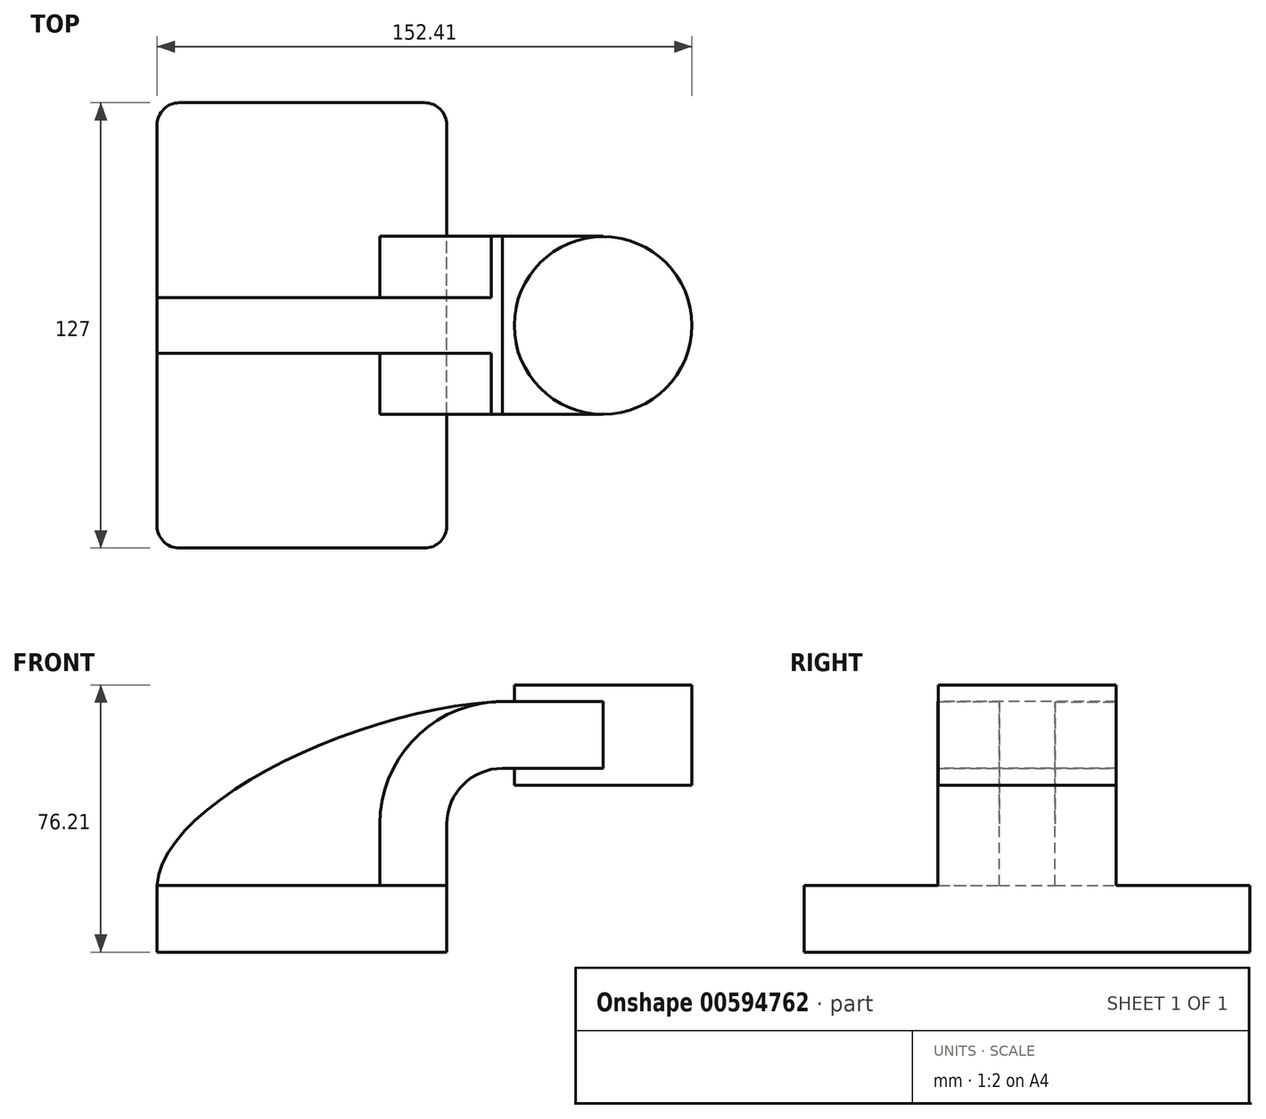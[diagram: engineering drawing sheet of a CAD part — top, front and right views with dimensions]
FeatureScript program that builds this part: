
annotation { "Feature Type Name" : "Feature", "Feature Type Description" : "" }
export const myFeature = defineFeature(function(context is Context, id is Id, definition is map)
    precondition{}
    {
        {
            var Q0;
            Q0=qCreatedBy(makeId("Front.planeOp"),FACE);
            var sketch = newSketch(context, id + "F0", { "sketchPlane" : qUnion([Q0])});
            skLineSegment(sketch, "E0.bottom", {"start": v(41.27, 9.53) * mm, "end": v(-41.28, 9.53) * mm});
            skLineSegment(sketch, "E0.top", {"start": v(41.28, -9.52) * mm, "end": v(-41.27, -9.52) * mm});
            skLineSegment(sketch, "E0.left", {"start": v(41.28, 9.53) * mm, "end": v(41.28, -9.52) * mm});
            skLineSegment(sketch, "E0.right", {"start": v(-41.28, 9.53) * mm, "end": v(-41.27, -9.52) * mm});
            skPoint(sketch, "E0.middle", {"position": v(0, 0) * mm});
            skLineSegment(sketch, "E1.bottom", {"start": v(60.32, 38.1) * mm, "end": v(111.12, 38.1) * mm});
            skLineSegment(sketch, "E1.top", {"start": v(60.32, 66.68) * mm, "end": v(111.12, 66.68) * mm});
            skLineSegment(sketch, "E1.left", {"start": v(60.32, 38.1) * mm, "end": v(60.32, 66.67) * mm});
            skLineSegment(sketch, "E1.right", {"start": v(111.12, 38.1) * mm, "end": v(111.12, 66.68) * mm});
            skPoint(sketch, "E1.middle", {"position": v(85.72, 52.39) * mm});
            skLineSegment(sketch, "E2", {"start": v(41.27, 9.53) * mm, "end": v(41.27, 27) * mm});
            skArc(sketch, "E3", {"start": v(41.27, 27) * mm, "mid": v(45.92, 38.23) * mm, "end": v(57.15, 42.88) * mm});
            skLineSegment(sketch, "E4", {"start": v(57.15, 42.88) * mm, "end": v(85.8, 42.88) * mm});
            skArc(sketch, "E5.0", {"start": v(22.22, 27) * mm, "mid": v(32.45, 51.7) * mm, "end": v(57.15, 61.93) * mm});
            skLineSegment(sketch, "E5.1", {"start": v(22.22, 9.53) * mm, "end": v(22.22, 27) * mm});
            skLineSegment(sketch, "E6.0", {"start": v(57.15, 61.93) * mm, "end": v(85.8, 61.93) * mm});
            skLineSegment(sketch, "E7", {"start": v(85.8, 61.93) * mm, "end": v(85.8, 66.68) * mm});
            skLineSegment(sketch, "E8", {"start": v(85.8, 66.68) * mm, "end": v(85.8, 61.93) * mm});
            skLineSegment(sketch, "E9", {"start": v(85.8, 66.68) * mm, "end": v(85.8, 38.1) * mm});
            skFitSpline(sketch, "E10", {"points": [v(-41.28, 9.53) * mm, v(57.15, 61.93) * mm], "startDerivative": vector(4.3, 72.88) * mm, "endDerivative": vector(115.36, 3.24) * mm});
            skSolve(sketch);
        }
        {
            var Q0;
            Q0=makeQuery(id+"F0.imprint","IMPRINT",FACE,{"disambiguationData":[TD([[makeQuery(id+"F0.imprint","IMPRINT",EDGE,{"derivedFrom":sQuery(id+"F0.wireOp",EDGE,"E0.top")}),-1.0]])]});
            extrude(context, id + "F1", {"entities" : qUnion([Q0]), "endBound" : BoundingType.SYMMETRIC, "depth" : 127 * mm, "offsetDistance" : 25.4 * mm});
        }
        {
            var Q0;
            {var subQ1=sQuery(id+"F0.wireOp",EDGE,"E2");Q0=makeQuery(id+"F0.imprint","IMPRINT",FACE,{"disambiguationData":[TD([[makeQuery(id+"F0.imprint","IMPRINT",EDGE,{"derivedFrom":subQ1}),1.0]])]});}
            var Q1;
            {var subQ0=sQuery(id+"F0.wireOp",EDGE,"E4");var subQ1=sQuery(id+"F0.wireOp",EDGE,"E1.left");var subQ2=makeQuery(id+"F0.imprint","INTERSECT",VERTEX,{"derivedFrom":[subQ1,subQ0]});Q1=makeQuery(id+"F0.imprint","IMPRINT",FACE,{"disambiguationData":[TD([[makeQuery(id+"F0.imprint","IMPRINT",EDGE,{"disambiguationData":[TD([[subQ2,-1.0]])],"derivedFrom":subQ1}),-1.0]])]});}
            extrude(context, id + "F2", {"entities" : qUnion([Q0, Q1]), "operationType" : NewBodyOperationType.ADD, "endBound" : BoundingType.SYMMETRIC, "depth" : 50.8 * mm, "offsetDistance" : 25.4 * mm});
        }
        {
            var Q0;
            {var subQ3=sQuery(id+"F0.wireOp",EDGE,"E5.1");Q0=makeQuery(id+"F0.imprint","IMPRINT",FACE,{"disambiguationData":[TD([[makeQuery(id+"F0.imprint","IMPRINT",EDGE,{"derivedFrom":subQ3}),1.0]])]});}
            extrude(context, id + "F3", {"entities" : qUnion([Q0]), "operationType" : NewBodyOperationType.ADD, "endBound" : BoundingType.SYMMETRIC, "depth" : 15.88 * mm, "offsetDistance" : 25.4 * mm});
        }
        {
            var Q0;
            {var subQ4=sQuery(id+"F0.wireOp",EDGE,"E1.right");Q0=makeQuery(id+"F0.imprint","IMPRINT",FACE,{"disambiguationData":[TD([[makeQuery(id+"F0.imprint","IMPRINT",EDGE,{"derivedFrom":subQ4}),1.0]])]});}
            var Q1;
            Q1=sQuery(id+"F0.wireOp",EDGE,"E9");
            revolve(context, id + "F4", {"operationType" : NewBodyOperationType.ADD, "entities" : qUnion([Q0]), "axis" : qUnion([Q1]), "revolveType" : RevolveType.FULL});
        }
        {
            var Q0;
            Q0=makeQuery(id+"F1.opExtrude","CAP_EDGE",EDGE,{"disambiguationData":[OSD([sQuery(id+"F0.wireOp",EDGE,"E0.left")])],"isStart":false});
            var Q1;
            Q1=makeQuery(id+"F1.opExtrude","CAP_EDGE",EDGE,{"disambiguationData":[OSD([sQuery(id+"F0.wireOp",EDGE,"E0.right")])],"isStart":false});
            var Q2;
            Q2=makeQuery(id+"F1.opExtrude","CAP_EDGE",EDGE,{"disambiguationData":[OSD([sQuery(id+"F0.wireOp",EDGE,"E0.left")])],"isStart":true});
            var Q3;
            Q3=makeQuery(id+"F1.opExtrude","CAP_EDGE",EDGE,{"disambiguationData":[OSD([sQuery(id+"F0.wireOp",EDGE,"E0.right")])],"isStart":true});
            fillet(context, id + "F5", {"entities" : qUnion([Q0, Q1, Q2, Q3]), "radius" : 6.35 * mm, "tangentPropagation" : true, "allowEdgeOverflow" : false});
        }
    });
